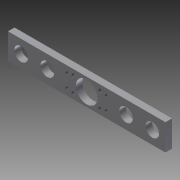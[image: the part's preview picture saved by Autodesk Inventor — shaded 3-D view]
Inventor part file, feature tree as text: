
AUTODESK INVENTOR PART (.ipt)
format: ipt  version: 2011 (Build 150239000, 239)  size: 128,000 bytes
history: native  units: in
note: dims shown in document units (in); Inventor stores cm internally (conversion verified against a paired STEP export)
features: sketch x7, hole x3, extrude x2, plane x2, mirror x2
ambient origin geometry x8: Origin, YZ Plane, XZ Plane, XY Plane, X Axis, Y Axis, Z Axis, Center Point
bodies: Solid1 (feature_tree)
feature tree (16):
  extrude  "Extrusion1"  Depth=0.374in
  extrude  "Extrusion2"  Depth=3.0in
  hole  "Hole1"  [1 undecoded]
  sketch  "Sketch5"  dims[d7=0.4134in d8=0.0625in d9=0.0in]
  plane  "Work Plane1"
  mirror  "Mirror1"
  hole  "Hole2"  [1 undecoded]
  sketch  "Sketch7"  dims[d15=120.0deg]
  plane  "Work Plane2"
  mirror  "Mirror2"
  hole  "Hole3"  [1 undecoded]
  sketch  "Sketch1"  dims[d0=0.51in d1=0.374in]
  sketch  "Sketch2"  dims[d2=0.75in d3=3.0in]
  sketch  "Sketch4"  dims[d4=0.5in d5=0.125in d6=0.0in]
  sketch  "Sketch6"  dims[d13=0.5906in d14=30.0deg]
  sketch  "Sketch8"  dims[d16=0.067in d17=0.75in d18=0.375in d19=0.25in d20=0.5635in d21=0.0315in d22=0.8108in d23=90.0deg d24=0.26in d25=0.75in d26=0.375in d27=0.25in d28=0.5635in d29=0.0315in d30=0.8108in d31=90.0deg d32=0.062in d33=0.75in d34=0.375in d35=0.25in d36=0.5635in d37=0.0315in d38=0.8108in]
note: 3 required parameter values undecoded (feature->parameter linkage not recoverable at this tier; creation-order binding heuristic only, values carry confidence <= 0.55)
